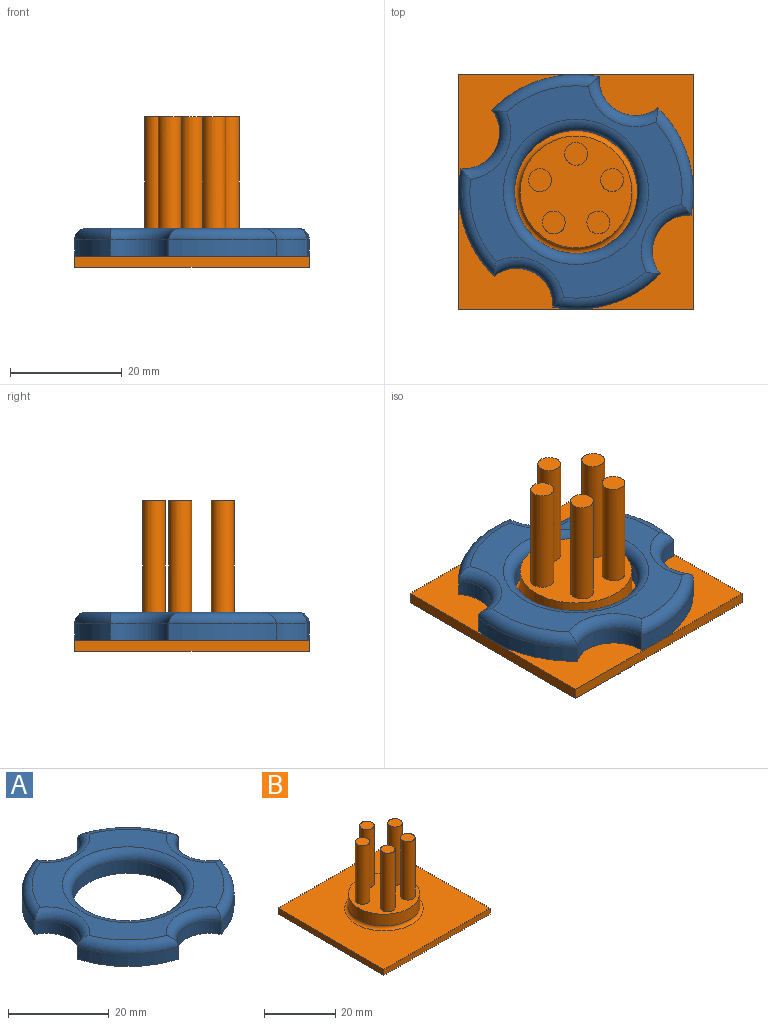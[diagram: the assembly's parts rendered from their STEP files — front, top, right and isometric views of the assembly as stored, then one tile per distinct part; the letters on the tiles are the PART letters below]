
ASSEMBLY  parts=2 mates=1
PART A: 20 faces, bbox 43.6x43.6x5 mm
  f0: cylinder r=21mm len=14.2mm, axis (0,0,-1), area 62.8mm2, adj f1,f7,f10,f18
  f1: plane 40.28x40.28mm, normal (0,0,-1), area 846.6mm2, adj f0,f2,f3,f4,f5,f7,f8,f9
  f2: cylinder r=21mm len=14.2mm, axis (0,0,-1), area 62.8mm2, adj f1,f9,f10,f14
  f3: cylinder r=21mm len=14.2mm, axis (0,0,-1), area 62.8mm2, adj f1,f8,f9,f11
  f4: cylinder r=21mm len=14.2mm, axis (0,0,-1), area 62.8mm2, adj f1,f7,f8,f15
  f5: cylinder r=11mm len=22mm, axis (0,0,-1), area 207.3mm2, adj f1,f19
  f6: plane 35.46x35.46mm, normal (0,0,1), area 425.6mm2, adj f11,f12,f13,f14,f15,f16,f17,f18
  f7: cylinder r=6.52mm len=11.89mm, axis (0,0,1), area 44.9mm2, adj f0,f1,f4,f17
  f8: cylinder r=6.52mm len=11.89mm, axis (0,0,1), area 44.9mm2, adj f1,f3,f4,f13
  f9: cylinder r=6.52mm len=11.89mm, axis (0,0,1), area 44.9mm2, adj f1,f2,f3,f12
  f10: cylinder r=6.52mm len=11.89mm, axis (0,0,1), area 44.9mm2, adj f0,f1,f2,f16
  f11: torus R=19mm, axis (0,0,1), area 59.8mm2, adj f3,f6,f12,f13
  f12: torus R=8.52mm, axis (0,0,1), area 48.1mm2, adj f6,f9,f11,f14
  f13: torus R=8.52mm, axis (0,0,1), area 48.1mm2, adj f6,f8,f11,f15
  f14: torus R=19mm, axis (0,0,1), area 59.8mm2, adj f2,f6,f12,f16
  f15: torus R=19mm, axis (0,0,1), area 59.8mm2, adj f4,f6,f13,f17
  f16: torus R=8.52mm, axis (0,0,1), area 48.1mm2, adj f6,f10,f14,f18
  f17: torus R=8.52mm, axis (0,0,1), area 48.1mm2, adj f6,f7,f15,f18
  f18: torus R=19mm, axis (0,0,1), area 59.8mm2, adj f0,f6,f16,f17
  f19: torus R=13mm, axis (0,0,1), area 231.5mm2, adj f5,f6
PART B: 19 faces, bbox 42x42x27 mm
  f0: plane 42x2mm, normal (1,0,0), area 84mm2, adj f1,f3,f4,f5
  f1: plane 42x2mm, normal (0,1,0), area 84mm2, adj f0,f2,f4,f5
  f2: plane 42x2mm, normal (-1,0,0), area 84mm2, adj f1,f3,f4,f5
  f3: plane 42x2mm, normal (0,-1,0), area 84mm2, adj f0,f2,f4,f5
  f4: plane 42x42mm, normal (0,0,-1), area 1764mm2, adj f0,f1,f2,f3
  f5: plane 42x42mm, normal (0,0,1), area 1383.9mm2, adj f0,f1,f2,f3,f8
  f6: cylinder r=10mm len=20mm, axis (0,0,-1), area 251.3mm2, adj f7,f8
  f7: plane 20x20mm, normal (0,0,1), area 249.2mm2, adj f6,f9,f11,f13,f15,f17
  f8: torus R=11mm, axis (0,0,1), area 102.3mm2, adj f5,f6
  f9: cylinder r=2.03mm len=20mm, axis (0,0,-1), area 255.6mm2, adj f7,f10
  f10: plane 4.07x4.07mm, normal (0,0,1), area 13mm2, adj f9
  f11: cylinder r=2.03mm len=20mm, axis (0,0,-1), area 255.6mm2, adj f7,f12
  f12: plane 4.07x4.07mm, normal (0,0,1), area 13mm2, adj f11
  f13: cylinder r=2.03mm len=20mm, axis (0,0,-1), area 255.6mm2, adj f7,f14
  f14: plane 4.07x4.07mm, normal (0,0,1), area 13mm2, adj f13
  f15: cylinder r=2.03mm len=20mm, axis (0,0,-1), area 255.6mm2, adj f7,f16
  f16: plane 4.07x4.07mm, normal (0,0,1), area 13mm2, adj f15
  f17: cylinder r=2.03mm len=20mm, axis (0,0,-1), area 255.6mm2, adj f7,f18
  f18: plane 4.07x4.07mm, normal (0,0,1), area 13mm2, adj f17
PLACE A rot(axis=(0,0,1),62.2deg) t=(-21,21,2)mm
PLACE B t=(-21,21,2)mm fixed
MATE revolute B.f6 <-> A.f0  axis (0,0,1) through (-21,21,2)mm
